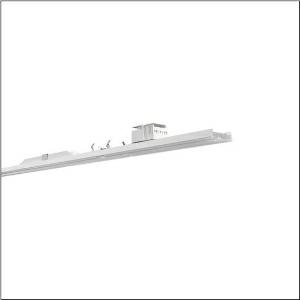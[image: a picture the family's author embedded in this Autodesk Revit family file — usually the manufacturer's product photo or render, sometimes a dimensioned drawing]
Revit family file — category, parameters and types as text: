
# Revit family: licross_r__11_recessed_mo_51tl12dn49xfd_5830
name_source: partatom
category: Lighting Fixtures
units: mm (PartAtom-declared; Revit-internal decimal feet)

## family parameters
Cut with Voids When Loaded = No
Host = Face
Light Source = No
Part Type = Normal
Room Calculation Point = No
Round Connector Dimension = Use Diameter
Shared = No

## types (1)
- --- (1 x LED, 1460 lm, 9.8 W, 4000K)
    Apparent Load = 10 VA
    CIE Flux Codes = 67 92 99 100 100
    Color Rendering = 80
    Color Temperature = 4000K
    Default Elevation = 1800 mm
    Description = Licross® 11 Recessed MOluminaire insert, length: 1.500mm, width: 66mm, height: 67mm, LED rated luminous flux: 9.140lm, light colour: 840, control gear: DALI 2, control gear: ECG DALI, with plug, 6-pole, with phase selection, mains connection: 220..240V, AC/DC, 0/50..60Hz, without changeover relay, for emergency light function, for central battery installations according to DIN EN 60598-2-22, halogen-free wiring, primary optical cover: cover, of PMMA, light emission: direct distribution, protection rating (complete): IP40, insulation class (complete): insulation class I (protective earthing), certification: CE, ENEC, VDE, protection symbol: D if used in an environment without relevant dust loads with corresponding accessories, permissible ambient temperature for indoor applications: -25..+40°C, standard: EN 60598-2-22, reducing of maximum allowable ambient temperature of 5°C with ceiling mounting, corresponds to IFS (International Featured Standards) requirements for safety and quality in the food industry, packaging unit: 1 piece
    Height = 58 mm
    Lamp = 1 x LED
    Lamp Light Flux = 1460 lm
    Lamp Power = 9.8 W
    Lamp count = 1
    Length = 1500 mm
    Luminous efficacy = 149 lm/W
    Manufacturer = Siteco
    ModVariant = No
    Model = 51TL12DN49XFD
    Mounting Place = Ceiling
    Mounting Type = Pendant
    Number of Poles = 1
    OnlyDefault = Yes
    Power Factor = 1
    Product Name = Licross® 11 Recessed MO
    Product group = luminaire insert
    ProductGroupID = 902
    Protection Class = Protection class I
    Protection Degree = IP 40
    RLX_Detail_Level = 1
    RlxData = <blob elided: 22561 chars, md5=d437188f>
    Socket = socket
    Standby Power = 0 W
    System Light Flux = 1460 lm
    System Power = 10 W
    Type Comments = : DC mode (central or group accumulator) initial emergency light level
    Type Image = l_1266722.jpg
    URL = http://relux.com
    VarID = @adj_134409
    Voltage = 0 V
    Weight = 0.00 kg
    Width = 66 mm

## geometry (parser evidence)
native form markers: Blend x4, Sweep x12
no freeform markers — native parametric forms only
